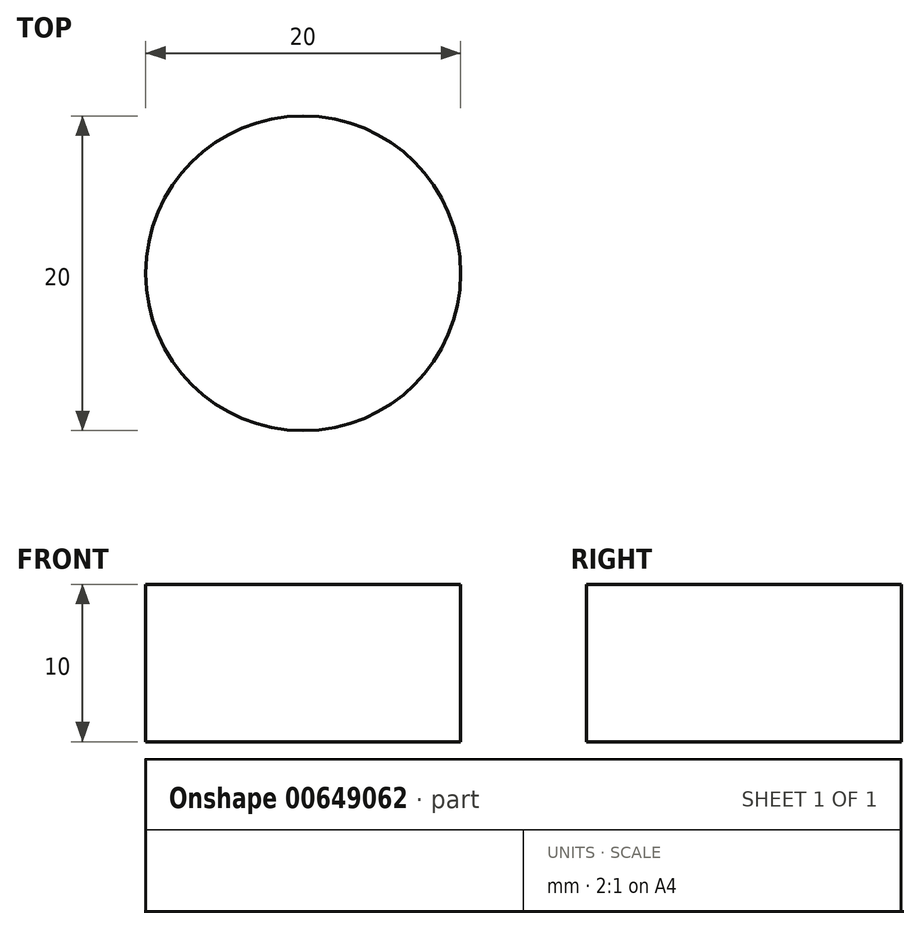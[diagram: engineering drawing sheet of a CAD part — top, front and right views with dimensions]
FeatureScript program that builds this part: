
annotation { "Feature Type Name" : "Feature", "Feature Type Description" : "" }
export const myFeature = defineFeature(function(context is Context, id is Id, definition is map)
    precondition{}
    {
        {
            var Q0;
            Q0=qCreatedBy(makeId("Top.planeOp"),FACE);
            var sketch = newSketch(context, id + "F0", { "sketchPlane" : qUnion([Q0])});
            skCircle(sketch, "E0", {"center": v(0, 0) * mm, "radius": 10 * mm});
            skSolve(sketch);
        }
        {
            var Q0;
            Q0=makeQuery(id+"F0.imprint","IMPRINT",FACE,{"disambiguationData":[TD([[makeQuery(id+"F0.imprint","IMPRINT",EDGE,{"derivedFrom":sQuery(id+"F0.wireOp",EDGE,"E0")}),1.0]])]});
            extrude(context, id + "F1", {"entities" : qUnion([Q0]), "depth" : 10 * mm, "offsetDistance" : 25 * mm});
        }
    });
